# Revit family: Safety-Railing_Section_SafetyRail_Standalone-SelfClosingGate
name_source: partatom
category: Railings
units: mm (PartAtom-declared; Revit-internal decimal feet)

## family parameters
Classification Number = 23.30.80.11
Cut with Voids When Loaded = No
Shared = No

## types (7) — shared parameters
Construction Details = http://www.arcat.com
Description = Safety Rail Company Adjustable Self-Closing Gate as Specified
Green Building-LEED = http://www.arcat.com
Keynote = 05 52 00
Manufacturer = Safety Rail Company
Manufacturer Fax = 888-471-4931
Manufacturer Website = http://www.safetyrailcompany.com
Product Data = http://www.arcat.com
Product Properties = http://www.safetyrailcompany.com
Revision = R1_2017-08
Sales Information = http://www.safetyrailcompany.com
SpecWizard = http://www.arcat.com
Specification = http://www.arcat.com
Standards Conformance = OSHA 29 CFR 1910.23(a)(2)  ;  Made in USA
URL = http://www.safetyrailcompany.com
Unit Height = 3' - 6"
zero-valued in all types: Expected Lifespan (Years), Maintenance Schedule (Months), Warranty Duration (Years)

## per-type parameters (varying)
| type | Clear Width Max | Clear Width Min | Gate Width Ranges | Model |
| Flat Attached 33-39 in | 3' - 3" | 2' - 9" | FlatAttachment : 33-39 | SCG Flat |
| Flat Attached 26-32 in | 2' - 8" | 2' - 2" | FlatAttachment : 26-32 | SCG Flat |
| Flat Attached 19-25 in | 2' - 1" | 1' - 7" | FlatAttachment : 19-25 | SCG Flat |
| Flat Attached 16-22 in | 1' - 10" | 1' - 4" | FlatAttachment : 16-22 | SCG Flat |
| Post Attached 30-36 in | 3' - 0" | 2' - 6" | PostAttachment : 30-36 | SCG Post |
| Post Attached 23-29 in | 2' - 5" | 1' - 11" | PostAttachment : 23-29 | SCG Post |
| Post Attached 16-22 in | 1' - 10" | 1' - 4" | PostAttachment : 16-22 | SCG Post |

## geometry (parser evidence)
native form markers: Sweep x6
no freeform markers — native parametric forms only
